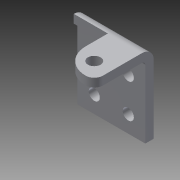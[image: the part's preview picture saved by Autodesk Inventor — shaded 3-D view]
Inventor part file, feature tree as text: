
AUTODESK INVENTOR PART (.ipt)
format: ipt  version: 2014 (Build 180170000, 170)  size: 199,680 bytes
history: native  units: in
note: dims shown in document units (in); Inventor stores cm internally (conversion verified against a paired STEP export)
features: sheet_metal_op x4, sketch x3, other x3, extrude x1, fillet x1
ambient origin geometry x8: Origin, YZ Plane, XZ Plane, XY Plane, X Axis, Y Axis, Z Axis, Center Point
bodies: Solid1 (feature_tree)
feature tree (12):
  sheet_metal_op  "Face1"
  sheet_metal_op  "Flange1"
  extrude  "Extrusion1"  Depth=1.0in
  fillet  "Fillet1"  Radius=0.164in
  sketch  "Sketch1"  dims[d0=1.0in d1=1.0in d2=0.164in]
  other  "Plate1"
  sketch  "Sketch2"  dims[d3=0.25in]
  other  "Plate2"
  sheet_metal_op  "Bend1"
  sheet_metal_op  "Corner1"
  sketch  "Sketch3"  dims[d4=0.25in d5=0.7874in d7=0.5in d8=0.7874in d10=0.5in d13=0.125in d14=0.125in d15=0.0625in d16=0.25in d17=0.125in d18=0.875in d19=90.0deg d20=0.05in d21=0.5in d22=0.125in d23=0.125in d24=0.187in d25=0.25in d26=0.25in d27=0.375in d28=0.125in d29=0.5in d30=1.0in d31=0.0in d32=0.125in]
  other  "Definition1"
